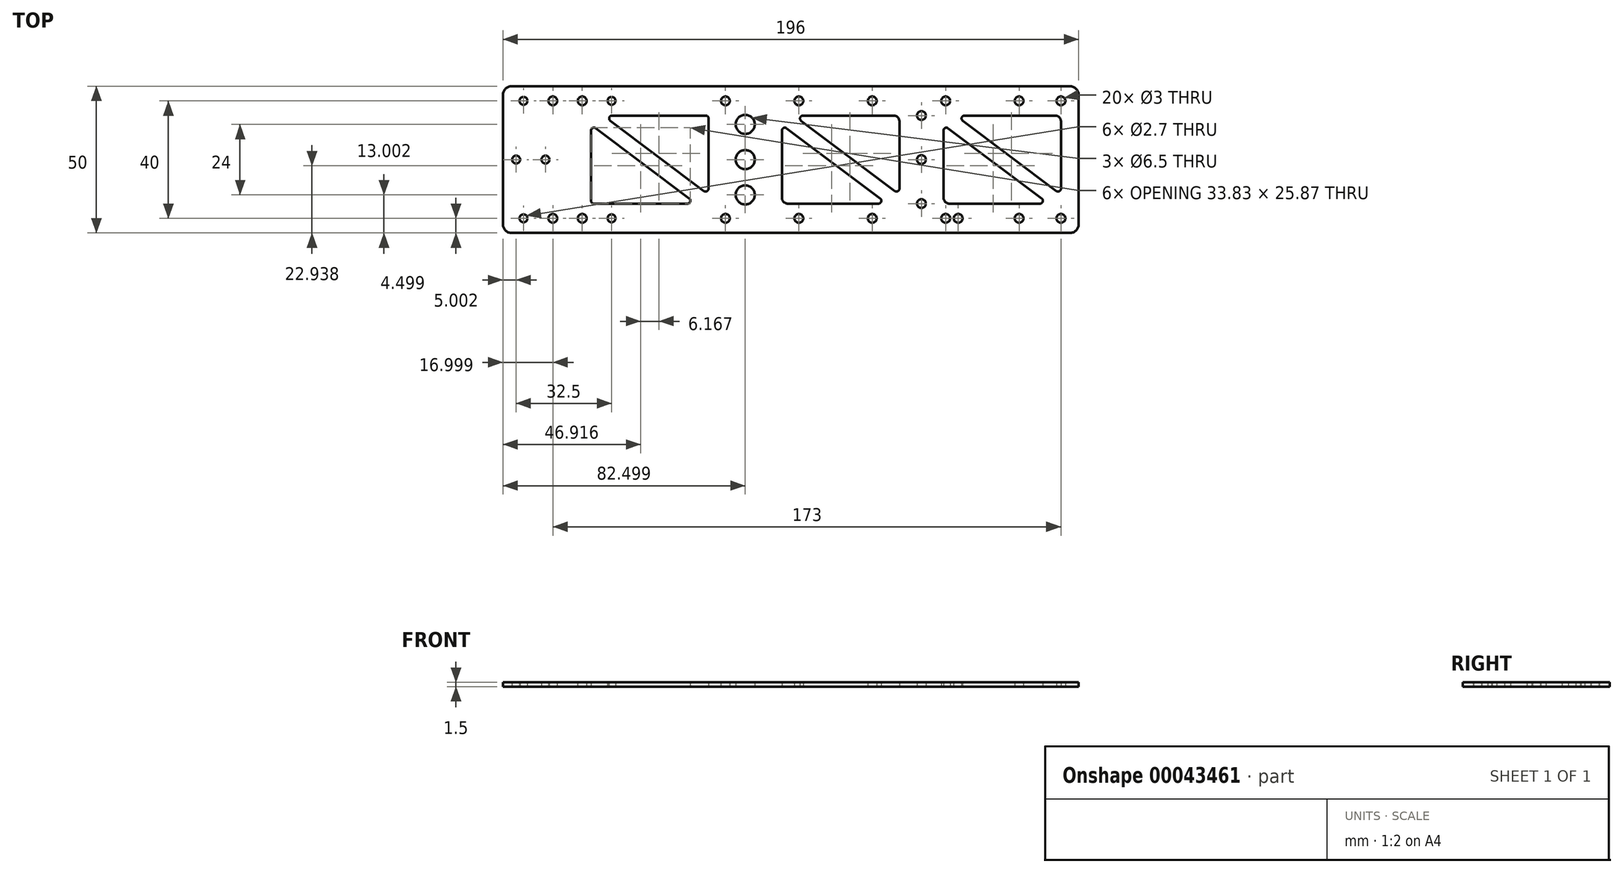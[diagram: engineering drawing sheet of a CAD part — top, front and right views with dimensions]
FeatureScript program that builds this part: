
annotation { "Feature Type Name" : "Feature", "Feature Type Description" : "" }
export const myFeature = defineFeature(function(context is Context, id is Id, definition is map)
    precondition{}
    {
        {
            var Q0;
            Q0=qCreatedBy(makeId("Top.planeOp"),FACE);
            var sketch = newSketch(context, id + "F0", { "sketchPlane" : qUnion([Q0])});
            skLineSegment(sketch, "E0.bottom", {"start": v(-128.11, 727.82) * mm, "end": v(61.89, 727.82) * mm});
            skLineSegment(sketch, "E0.top", {"start": v(-128.11, 677.82) * mm, "end": v(61.89, 677.82) * mm});
            skLineSegment(sketch, "E0.left", {"start": v(-131.11, 724.82) * mm, "end": v(-131.11, 680.82) * mm});
            skLineSegment(sketch, "E0.right", {"start": v(64.89, 724.82) * mm, "end": v(64.89, 680.82) * mm});
            skLineSegment(sketch, "E1", {"start": v(-131.11, 702.82) * mm, "end": v(64.89, 702.82) * mm});
            skCircle(sketch, "E2", {"center": v(-114.11, 722.82) * mm, "radius": 1.5 * mm});
            skCircle(sketch, "E3", {"center": v(-55.36, 722.82) * mm, "radius": 1.5 * mm});
            skCircle(sketch, "E4", {"center": v(23.89, 722.82) * mm, "radius": 1.5 * mm});
            skCircle(sketch, "E5", {"center": v(58.89, 722.82) * mm, "radius": 1.5 * mm});
            skCircle(sketch, "E6.MirrorC", {"center": v(58.89, 682.82) * mm, "radius": 1.5 * mm});
            skCircle(sketch, "E7.MirrorC", {"center": v(23.89, 682.82) * mm, "radius": 1.5 * mm});
            skCircle(sketch, "E8.MirrorC", {"center": v(-55.36, 682.82) * mm, "radius": 1.5 * mm});
            skCircle(sketch, "E9.MirrorC", {"center": v(-114.11, 682.82) * mm, "radius": 1.5 * mm});
            skCircle(sketch, "E10.MirrorC", {"center": v(-94.11, 682.82) * mm, "radius": 1.35 * mm});
            skPoint(sketch, "E11.visualSharp", {"position": v(64.89, 727.82) * mm});
            skArc(sketch, "E11.filletArc", {"start": v(64.89, 724.82) * mm, "mid": v(64.01, 726.94) * mm, "end": v(61.89, 727.82) * mm});
            skPoint(sketch, "E12.visualSharp", {"position": v(64.89, 677.82) * mm});
            skArc(sketch, "E12.filletArc", {"start": v(61.89, 677.82) * mm, "mid": v(64.01, 678.7) * mm, "end": v(64.89, 680.82) * mm});
            skLineSegment(sketch, "E13.bottom", {"start": v(56.89, 717.82) * mm, "end": v(20.89, 717.82) * mm});
            skLineSegment(sketch, "E13.top", {"start": v(56.89, 687.82) * mm, "end": v(20.89, 687.82) * mm});
            skLineSegment(sketch, "E13.left", {"start": v(58.89, 715.82) * mm, "end": v(58.89, 689.82) * mm});
            skLineSegment(sketch, "E13.right", {"start": v(18.89, 715.82) * mm, "end": v(18.89, 689.82) * mm});
            skLineSegment(sketch, "E14.bottom", {"start": v(1.89, 717.82) * mm, "end": v(-34.11, 717.82) * mm});
            skLineSegment(sketch, "E14.top", {"start": v(1.89, 687.82) * mm, "end": v(-34.11, 687.82) * mm});
            skLineSegment(sketch, "E14.left", {"start": v(3.89, 715.82) * mm, "end": v(3.89, 689.82) * mm});
            skLineSegment(sketch, "E14.right", {"start": v(-36.11, 715.82) * mm, "end": v(-36.11, 689.82) * mm});
            skLineSegment(sketch, "E15.bottom", {"start": v(-62.11, 717.82) * mm, "end": v(-98.11, 717.82) * mm});
            skLineSegment(sketch, "E15.top", {"start": v(-64.11, 687.82) * mm, "end": v(-100.11, 687.82) * mm});
            skLineSegment(sketch, "E15.left", {"start": v(-61.11, 716.82) * mm, "end": v(-61.11, 690.82) * mm});
            skLineSegment(sketch, "E15.right", {"start": v(-101.11, 714.82) * mm, "end": v(-101.11, 688.82) * mm});
            skPoint(sketch, "E16.visualSharp", {"position": v(-101.11, 717.82) * mm});
            skArc(sketch, "E16.filletArc", {"start": v(-98.11, 717.82) * mm, "mid": v(-100.23, 716.94) * mm, "end": v(-101.11, 714.82) * mm});
            skPoint(sketch, "E17.visualSharp", {"position": v(-101.11, 687.82) * mm});
            skArc(sketch, "E17.filletArc", {"start": v(-101.11, 688.82) * mm, "mid": v(-100.82, 688.12) * mm, "end": v(-100.11, 687.82) * mm});
            skPoint(sketch, "E18.visualSharp", {"position": v(-131.11, 727.82) * mm});
            skArc(sketch, "E18.filletArc", {"start": v(-128.11, 727.82) * mm, "mid": v(-130.23, 726.94) * mm, "end": v(-131.11, 724.82) * mm});
            skPoint(sketch, "E19.visualSharp", {"position": v(-131.11, 677.82) * mm});
            skArc(sketch, "E19.filletArc", {"start": v(-131.11, 680.82) * mm, "mid": v(-130.23, 678.7) * mm, "end": v(-128.11, 677.82) * mm});
            skCircle(sketch, "E20", {"center": v(-124.11, 722.82) * mm, "radius": 1.35 * mm});
            skCircle(sketch, "E21", {"center": v(-104.11, 722.82) * mm, "radius": 1.5 * mm});
            skPoint(sketch, "E22.visualSharp", {"position": v(-61.11, 717.82) * mm});
            skArc(sketch, "E22.filletArc", {"start": v(-61.11, 716.82) * mm, "mid": v(-61.4, 717.53) * mm, "end": v(-62.11, 717.82) * mm});
            skPoint(sketch, "E23.visualSharp", {"position": v(-61.11, 687.82) * mm});
            skArc(sketch, "E23.filletArc", {"start": v(-64.11, 687.82) * mm, "mid": v(-61.99, 688.7) * mm, "end": v(-61.11, 690.82) * mm});
            skCircle(sketch, "E24", {"center": v(-48.61, 714.82) * mm, "radius": 3.25 * mm});
            skCircle(sketch, "E25", {"center": v(-48.61, 702.82) * mm, "radius": 3.25 * mm});
            skCircle(sketch, "E26", {"center": v(-48.61, 690.82) * mm, "radius": 3.25 * mm});
            skLineSegment(sketch, "E27", {"start": v(-101.11, 717.82) * mm, "end": v(-61.11, 687.82) * mm});
            skLineSegment(sketch, "E28", {"start": v(-96.94, 717.82) * mm, "end": v(-61.11, 690.95) * mm});
            skLineSegment(sketch, "E29", {"start": v(-101.11, 714.7) * mm, "end": v(-65.28, 687.82) * mm});
            skCircle(sketch, "E30", {"center": v(-93.94, 716.82) * mm, "radius": 1 * mm});
            skCircle(sketch, "E31", {"center": v(-62.11, 692.95) * mm, "radius": 1 * mm});
            skCircle(sketch, "E32", {"center": v(-68.28, 688.82) * mm, "radius": 1 * mm});
            skCircle(sketch, "E33", {"center": v(-100.11, 712.7) * mm, "radius": 1 * mm});
            skCircle(sketch, "E34", {"center": v(11.39, 702.82) * mm, "radius": 1.5 * mm});
            skCircle(sketch, "E35", {"center": v(11.39, 717.82) * mm, "radius": 1.5 * mm});
            skCircle(sketch, "E36", {"center": v(11.39, 687.82) * mm, "radius": 1.5 * mm});
            skPoint(sketch, "E37.visualSharp", {"position": v(-36.11, 717.82) * mm});
            skArc(sketch, "E37.filletArc", {"start": v(-34.11, 717.82) * mm, "mid": v(-35.53, 717.24) * mm, "end": v(-36.11, 715.82) * mm});
            skPoint(sketch, "E38.visualSharp", {"position": v(-36.11, 687.82) * mm});
            skArc(sketch, "E38.filletArc", {"start": v(-36.11, 689.82) * mm, "mid": v(-35.53, 688.4) * mm, "end": v(-34.11, 687.82) * mm});
            skPoint(sketch, "E39.visualSharp", {"position": v(3.89, 717.82) * mm});
            skArc(sketch, "E39.filletArc", {"start": v(3.89, 715.82) * mm, "mid": v(3.3, 717.24) * mm, "end": v(1.89, 717.82) * mm});
            skPoint(sketch, "E40.visualSharp", {"position": v(3.89, 687.82) * mm});
            skArc(sketch, "E40.filletArc", {"start": v(1.89, 687.82) * mm, "mid": v(3.3, 688.4) * mm, "end": v(3.89, 689.82) * mm});
            skPoint(sketch, "E41.visualSharp", {"position": v(18.89, 717.82) * mm});
            skArc(sketch, "E41.filletArc", {"start": v(20.89, 717.82) * mm, "mid": v(19.47, 717.24) * mm, "end": v(18.89, 715.82) * mm});
            skPoint(sketch, "E42.visualSharp", {"position": v(58.89, 717.82) * mm});
            skArc(sketch, "E42.filletArc", {"start": v(58.89, 715.82) * mm, "mid": v(58.3, 717.24) * mm, "end": v(56.89, 717.82) * mm});
            skPoint(sketch, "E43.visualSharp", {"position": v(18.89, 687.82) * mm});
            skArc(sketch, "E43.filletArc", {"start": v(18.89, 689.82) * mm, "mid": v(19.47, 688.4) * mm, "end": v(20.89, 687.82) * mm});
            skPoint(sketch, "E44.visualSharp", {"position": v(58.89, 687.82) * mm});
            skArc(sketch, "E44.filletArc", {"start": v(56.89, 687.82) * mm, "mid": v(58.3, 688.4) * mm, "end": v(58.89, 689.82) * mm});
            skLineSegment(sketch, "E45", {"start": v(-36.11, 717.82) * mm, "end": v(3.89, 687.82) * mm});
            skLineSegment(sketch, "E46", {"start": v(-31.94, 717.82) * mm, "end": v(3.89, 690.95) * mm});
            skLineSegment(sketch, "E47", {"start": v(-36.11, 714.7) * mm, "end": v(-0.28, 687.82) * mm});
            skLineSegment(sketch, "E48", {"start": v(18.89, 717.82) * mm, "end": v(58.89, 687.82) * mm});
            skLineSegment(sketch, "E49", {"start": v(23.06, 717.82) * mm, "end": v(58.89, 690.95) * mm});
            skLineSegment(sketch, "E50", {"start": v(18.89, 714.7) * mm, "end": v(54.72, 687.82) * mm});
            skCircle(sketch, "E51", {"center": v(-28.94, 716.82) * mm, "radius": 1 * mm});
            skCircle(sketch, "E52", {"center": v(2.89, 692.95) * mm, "radius": 1 * mm});
            skCircle(sketch, "E53", {"center": v(-35.11, 712.7) * mm, "radius": 1 * mm});
            skCircle(sketch, "E54", {"center": v(-3.28, 688.82) * mm, "radius": 1 * mm});
            skCircle(sketch, "E55", {"center": v(19.89, 712.7) * mm, "radius": 1 * mm});
            skCircle(sketch, "E56", {"center": v(26.06, 716.82) * mm, "radius": 1 * mm});
            skCircle(sketch, "E57", {"center": v(57.89, 692.95) * mm, "radius": 1 * mm});
            skCircle(sketch, "E58", {"center": v(51.72, 688.82) * mm, "radius": 1 * mm});
            skCircle(sketch, "E59.MirrorC", {"center": v(-124.11, 682.82) * mm, "radius": 1.35 * mm});
            skCircle(sketch, "E60.MirrorC", {"center": v(-104.11, 682.82) * mm, "radius": 1.5 * mm});
            skCircle(sketch, "E61", {"center": v(-30.36, 722.82) * mm, "radius": 1.5 * mm});
            skCircle(sketch, "E62", {"center": v(-5.36, 722.82) * mm, "radius": 1.5 * mm});
            skCircle(sketch, "E63", {"center": v(19.64, 722.82) * mm, "radius": 1.5 * mm});
            skCircle(sketch, "E64", {"center": v(44.64, 722.82) * mm, "radius": 1.5 * mm});
            skCircle(sketch, "E65.MirrorC", {"center": v(-30.36, 682.82) * mm, "radius": 1.5 * mm});
            skCircle(sketch, "E66.MirrorC", {"center": v(19.64, 682.82) * mm, "radius": 1.5 * mm});
            skCircle(sketch, "E67.MirrorC", {"center": v(44.64, 682.82) * mm, "radius": 1.5 * mm});
            skCircle(sketch, "E68.MirrorC", {"center": v(-5.36, 682.82) * mm, "radius": 1.5 * mm});
            skCircle(sketch, "E69", {"center": v(-94.11, 722.82) * mm, "radius": 1.35 * mm});
            skCircle(sketch, "E70", {"center": v(-116.61, 702.82) * mm, "radius": 1.35 * mm});
            skCircle(sketch, "E71", {"center": v(-126.61, 702.82) * mm, "radius": 1.35 * mm});
            skSolve(sketch);
        }
        {
            var Q0;
            Q0=qSketchRegion(id+"F0",true);
            var Q1;
            {var subQ2=sQuery(id+"F0.wireOp",EDGE,"54195129-87a9-453f-ad2e-ab01bb990cc77.MirrorCS");Q1=makeQuery(id+"F0.imprint","IMPRINT",FACE,{"disambiguationData":[TD([[makeQuery(id+"F0.imprint","IMPRINT",EDGE,{"derivedFrom":subQ2}),-1.0]])]});}
            var Q2;
            {var subQ2=sQuery(id+"F0.wireOp",EDGE,"54195129-87a9-453f-ad2e-ab01bb990cc712.MirrorCS");Q2=makeQuery(id+"F0.imprint","IMPRINT",FACE,{"disambiguationData":[TD([[makeQuery(id+"F0.imprint","IMPRINT",EDGE,{"derivedFrom":subQ2}),1.0]])]});}
            var Q3;
            {var subQ0=sQuery(id+"F0.wireOp",EDGE,"54195129-87a9-453f-ad2e-ab01bb990cc74.MirrorCS");Q3=makeQuery(id+"F0.imprint","IMPRINT",FACE,{"disambiguationData":[TD([[makeQuery(id+"F0.imprint","IMPRINT",EDGE,{"derivedFrom":subQ0}),1.0]])]});}
            var Q4;
            {var subQ0=sQuery(id+"F0.wireOp",EDGE,"54195129-87a9-453f-ad2e-ab01bb990cc78.MirrorCS");Q4=makeQuery(id+"F0.imprint","IMPRINT",FACE,{"disambiguationData":[TD([[makeQuery(id+"F0.imprint","IMPRINT",EDGE,{"derivedFrom":subQ0}),1.0]])]});}
            var Q5;
            {var subQ0=sQuery(id+"F0.wireOp",EDGE,"BcqDGKqa-283v-lT3W-7pAC-w2yEAsonch5c");Q5=makeQuery(id+"F0.imprint","IMPRINT",FACE,{"disambiguationData":[TD([[makeQuery(id+"F0.imprint","IMPRINT",EDGE,{"derivedFrom":subQ0}),-1.0]])]});}
            var Q6;
            {var subQ2=sQuery(id+"F0.wireOp",EDGE,"ShlW986k-ajFc-8yeV-3Gdn-sOu9Hpu2vA3Z");Q6=makeQuery(id+"F0.imprint","IMPRINT",FACE,{"disambiguationData":[TD([[makeQuery(id+"F0.imprint","IMPRINT",EDGE,{"derivedFrom":subQ2}),-1.0]])]});}
            var Q7;
            {var subQ2=sQuery(id+"F0.wireOp",EDGE,"w6zGlNOe-O8Z4-KzDY-468z-d0JdHNhxJH18");Q7=makeQuery(id+"F0.imprint","IMPRINT",FACE,{"disambiguationData":[TD([[makeQuery(id+"F0.imprint","IMPRINT",EDGE,{"derivedFrom":subQ2}),-1.0]])]});}
            var Q8;
            {var subQ0=sQuery(id+"F0.wireOp",EDGE,"v6rJk5rU-W7GU-l5Cy-b2Ia-JKdmIbJVq7ve");Q8=makeQuery(id+"F0.imprint","IMPRINT",FACE,{"disambiguationData":[TD([[makeQuery(id+"F0.imprint","IMPRINT",EDGE,{"derivedFrom":subQ0}),-1.0]])]});}
            var Q9;
            {var subQ0=sQuery(id+"F0.wireOp",EDGE,"e183a9b5-fc32-46b4-9d97-09565e521898.right");var subQ1=sQuery(id+"F0.wireOp",EDGE,"wU84TTQi-j5bG-VybG-7onn-GEVu1O6ivYgl");var subQ2=makeQuery(id+"F0.imprint","INTERSECT",VERTEX,{"derivedFrom":[subQ1,subQ0]});Q9=makeQuery(id+"F0.imprint","IMPRINT",FACE,{"disambiguationData":[TD([[makeQuery(id+"F0.imprint","IMPRINT",EDGE,{"disambiguationData":[TD([[subQ2,-1.0]])],"derivedFrom":subQ1}),-1.0]])]});}
            var Q10;
            {var subQ0=sQuery(id+"F0.wireOp",EDGE,"e183a9b5-fc32-46b4-9d97-09565e521898.right");var subQ1=sQuery(id+"F0.wireOp",EDGE,"wU84TTQi-j5bG-VybG-7onn-GEVu1O6ivYgl");var subQ2=makeQuery(id+"F0.imprint","INTERSECT",VERTEX,{"derivedFrom":[subQ1,subQ0]});Q10=makeQuery(id+"F0.imprint","IMPRINT",FACE,{"disambiguationData":[TD([[makeQuery(id+"F0.imprint","IMPRINT",EDGE,{"disambiguationData":[TD([[subQ2,-1.0]])],"derivedFrom":subQ1}),1.0]])]});}
            var Q11;
            Q11=makeQuery(id+"F0.imprint","IMPRINT",FACE,{"disambiguationData":[TD([[makeQuery(id+"F0.imprint","IMPRINT",EDGE,{"derivedFrom":sQuery(id+"F0.wireOp",EDGE,"E4")}),1.0]])]});
            var Q12;
            Q12=makeQuery(id+"F0.imprint","IMPRINT",FACE,{"disambiguationData":[TD([[makeQuery(id+"F0.imprint","IMPRINT",EDGE,{"derivedFrom":sQuery(id+"F0.wireOp",EDGE,"E7.MirrorC")}),-1.0]])]});
            var Q13;
            {var subQ0=sQuery(id+"F0.wireOp",EDGE,"E29");var subQ6=sQuery(id+"F0.wireOp",EDGE,"E1");var subQ8=makeQuery(id+"F0.imprint","INTERSECT",VERTEX,{"derivedFrom":[subQ6,subQ0]});Q13=makeQuery(id+"F0.imprint","IMPRINT",FACE,{"disambiguationData":[TD([[makeQuery(id+"F0.imprint","IMPRINT",EDGE,{"disambiguationData":[TD([[subQ8,-1.0]])],"derivedFrom":subQ6}),1.0]])]});}
            var Q14;
            {var subQ0=sQuery(id+"F0.wireOp",EDGE,"E27");var subQ3=sQuery(id+"F0.wireOp",EDGE,"E1");var subQ4=makeQuery(id+"F0.imprint","INTERSECT",VERTEX,{"derivedFrom":[subQ3,subQ0]});Q14=makeQuery(id+"F0.imprint","IMPRINT",FACE,{"disambiguationData":[TD([[makeQuery(id+"F0.imprint","IMPRINT",EDGE,{"disambiguationData":[TD([[subQ4,-1.0]])],"derivedFrom":subQ3}),1.0]])]});}
            var Q15;
            {var subQ1=sQuery(id+"F0.wireOp",EDGE,"E1");var subQ4=sQuery(id+"F0.wireOp",EDGE,"E27");var subQ7=makeQuery(id+"F0.imprint","INTERSECT",VERTEX,{"derivedFrom":[subQ1,subQ4]});Q15=makeQuery(id+"F0.imprint","IMPRINT",FACE,{"disambiguationData":[TD([[makeQuery(id+"F0.imprint","IMPRINT",EDGE,{"disambiguationData":[TD([[subQ7,-1.0]])],"derivedFrom":subQ1}),-1.0]])]});}
            var Q16;
            {var subQ3=sQuery(id+"F0.wireOp",EDGE,"E1");var subQ7=sQuery(id+"F0.wireOp",EDGE,"E29");var subQ9=makeQuery(id+"F0.imprint","INTERSECT",VERTEX,{"derivedFrom":[subQ3,subQ7]});Q16=makeQuery(id+"F0.imprint","IMPRINT",FACE,{"disambiguationData":[TD([[makeQuery(id+"F0.imprint","IMPRINT",EDGE,{"disambiguationData":[TD([[subQ9,-1.0]])],"derivedFrom":subQ3}),-1.0]])]});}
            var Q17;
            {var subQ0=sQuery(id+"F0.wireOp",EDGE,"E23.filletArc");var subQ1=sQuery(id+"F0.wireOp",EDGE,"E15.left");var subQ2=makeQuery(id+"F0.imprint","INTERSECT",VERTEX,{"derivedFrom":[subQ1,subQ0]});Q17=makeQuery(id+"F0.imprint","IMPRINT",FACE,{"disambiguationData":[TD([[makeQuery(id+"F0.imprint","IMPRINT",EDGE,{"disambiguationData":[TD([[subQ2,1.0]])],"derivedFrom":subQ1}),-1.0]])]});}
            var Q18;
            {var subQ0=sQuery(id+"F0.wireOp",EDGE,"E29");var subQ1=sQuery(id+"F0.wireOp",EDGE,"E15.top");var subQ2=makeQuery(id+"F0.imprint","INTERSECT",VERTEX,{"derivedFrom":[subQ1,subQ0]});Q18=makeQuery(id+"F0.imprint","IMPRINT",FACE,{"disambiguationData":[TD([[makeQuery(id+"F0.imprint","IMPRINT",EDGE,{"disambiguationData":[TD([[subQ2,-1.0]])],"derivedFrom":subQ1}),-1.0]])]});}
            var Q19;
            {var subQ0=sQuery(id+"F0.wireOp",EDGE,"E28");var subQ1=sQuery(id+"F0.wireOp",EDGE,"E15.bottom");var subQ2=makeQuery(id+"F0.imprint","INTERSECT",VERTEX,{"derivedFrom":[subQ1,subQ0]});Q19=makeQuery(id+"F0.imprint","IMPRINT",FACE,{"disambiguationData":[TD([[makeQuery(id+"F0.imprint","IMPRINT",EDGE,{"disambiguationData":[TD([[subQ2,1.0]])],"derivedFrom":subQ1}),1.0]])]});}
            var Q20;
            {var subQ0=sQuery(id+"F0.wireOp",EDGE,"E16.filletArc");var subQ1=sQuery(id+"F0.wireOp",EDGE,"E15.right");var subQ2=makeQuery(id+"F0.imprint","INTERSECT",VERTEX,{"derivedFrom":[subQ1,subQ0]});Q20=makeQuery(id+"F0.imprint","IMPRINT",FACE,{"disambiguationData":[TD([[makeQuery(id+"F0.imprint","IMPRINT",EDGE,{"disambiguationData":[TD([[subQ2,-1.0]])],"derivedFrom":subQ1}),1.0]])]});}
            var Q21;
            {var subQ0=sQuery(id+"F0.wireOp",EDGE,"E45");var subQ3=sQuery(id+"F0.wireOp",EDGE,"E1");var subQ4=makeQuery(id+"F0.imprint","INTERSECT",VERTEX,{"derivedFrom":[subQ3,subQ0]});Q21=makeQuery(id+"F0.imprint","IMPRINT",FACE,{"disambiguationData":[TD([[makeQuery(id+"F0.imprint","IMPRINT",EDGE,{"disambiguationData":[TD([[subQ4,-1.0]])],"derivedFrom":subQ3}),1.0]])]});}
            var Q22;
            {var subQ3=sQuery(id+"F0.wireOp",EDGE,"E1");var subQ7=sQuery(id+"F0.wireOp",EDGE,"E47");var subQ9=makeQuery(id+"F0.imprint","INTERSECT",VERTEX,{"derivedFrom":[subQ3,subQ7]});Q22=makeQuery(id+"F0.imprint","IMPRINT",FACE,{"disambiguationData":[TD([[makeQuery(id+"F0.imprint","IMPRINT",EDGE,{"disambiguationData":[TD([[subQ9,-1.0]])],"derivedFrom":subQ3}),1.0]])]});}
            var Q23;
            {var subQ3=sQuery(id+"F0.wireOp",EDGE,"E1");var subQ7=sQuery(id+"F0.wireOp",EDGE,"E47");var subQ9=makeQuery(id+"F0.imprint","INTERSECT",VERTEX,{"derivedFrom":[subQ3,subQ7]});Q23=makeQuery(id+"F0.imprint","IMPRINT",FACE,{"disambiguationData":[TD([[makeQuery(id+"F0.imprint","IMPRINT",EDGE,{"disambiguationData":[TD([[subQ9,-1.0]])],"derivedFrom":subQ3}),-1.0]])]});}
            var Q24;
            {var subQ3=sQuery(id+"F0.wireOp",EDGE,"E45");var subQ7=sQuery(id+"F0.wireOp",EDGE,"E1");var subQ8=makeQuery(id+"F0.imprint","INTERSECT",VERTEX,{"derivedFrom":[subQ7,subQ3]});Q24=makeQuery(id+"F0.imprint","IMPRINT",FACE,{"disambiguationData":[TD([[makeQuery(id+"F0.imprint","IMPRINT",EDGE,{"disambiguationData":[TD([[subQ8,-1.0]])],"derivedFrom":subQ7}),-1.0]])]});}
            var Q25;
            {var subQ0=sQuery(id+"F0.wireOp",EDGE,"E47");var subQ1=sQuery(id+"F0.wireOp",EDGE,"E14.top");var subQ2=makeQuery(id+"F0.imprint","INTERSECT",VERTEX,{"derivedFrom":[subQ1,subQ0]});Q25=makeQuery(id+"F0.imprint","IMPRINT",FACE,{"disambiguationData":[TD([[makeQuery(id+"F0.imprint","IMPRINT",EDGE,{"disambiguationData":[TD([[subQ2,-1.0]])],"derivedFrom":subQ1}),-1.0]])]});}
            var Q26;
            {var subQ0=sQuery(id+"F0.wireOp",EDGE,"E46");var subQ1=sQuery(id+"F0.wireOp",EDGE,"E14.left");var subQ2=makeQuery(id+"F0.imprint","INTERSECT",VERTEX,{"derivedFrom":[subQ1,subQ0]});Q26=makeQuery(id+"F0.imprint","IMPRINT",FACE,{"disambiguationData":[TD([[makeQuery(id+"F0.imprint","IMPRINT",EDGE,{"disambiguationData":[TD([[subQ2,1.0]])],"derivedFrom":subQ1}),-1.0]])]});}
            var Q27;
            {var subQ0=sQuery(id+"F0.wireOp",EDGE,"E46");var subQ1=sQuery(id+"F0.wireOp",EDGE,"E14.bottom");var subQ2=makeQuery(id+"F0.imprint","INTERSECT",VERTEX,{"derivedFrom":[subQ1,subQ0]});Q27=makeQuery(id+"F0.imprint","IMPRINT",FACE,{"disambiguationData":[TD([[makeQuery(id+"F0.imprint","IMPRINT",EDGE,{"disambiguationData":[TD([[subQ2,1.0]])],"derivedFrom":subQ1}),1.0]])]});}
            var Q28;
            {var subQ0=sQuery(id+"F0.wireOp",EDGE,"E47");var subQ1=sQuery(id+"F0.wireOp",EDGE,"E14.right");var subQ2=makeQuery(id+"F0.imprint","INTERSECT",VERTEX,{"derivedFrom":[subQ1,subQ0]});Q28=makeQuery(id+"F0.imprint","IMPRINT",FACE,{"disambiguationData":[TD([[makeQuery(id+"F0.imprint","IMPRINT",EDGE,{"disambiguationData":[TD([[subQ2,-1.0]])],"derivedFrom":subQ1}),1.0]])]});}
            var Q29;
            {var subQ3=sQuery(id+"F0.wireOp",EDGE,"E1");var subQ5=sQuery(id+"F0.wireOp",EDGE,"E50");var subQ6=makeQuery(id+"F0.imprint","INTERSECT",VERTEX,{"derivedFrom":[subQ3,subQ5]});Q29=makeQuery(id+"F0.imprint","IMPRINT",FACE,{"disambiguationData":[TD([[makeQuery(id+"F0.imprint","IMPRINT",EDGE,{"disambiguationData":[TD([[subQ6,-1.0]])],"derivedFrom":subQ3}),1.0]])]});}
            var Q30;
            {var subQ0=sQuery(id+"F0.wireOp",EDGE,"E48");var subQ3=sQuery(id+"F0.wireOp",EDGE,"E1");var subQ4=makeQuery(id+"F0.imprint","INTERSECT",VERTEX,{"derivedFrom":[subQ3,subQ0]});Q30=makeQuery(id+"F0.imprint","IMPRINT",FACE,{"disambiguationData":[TD([[makeQuery(id+"F0.imprint","IMPRINT",EDGE,{"disambiguationData":[TD([[subQ4,-1.0]])],"derivedFrom":subQ3}),1.0]])]});}
            var Q31;
            {var subQ3=sQuery(id+"F0.wireOp",EDGE,"E1");var subQ5=sQuery(id+"F0.wireOp",EDGE,"E50");var subQ6=makeQuery(id+"F0.imprint","INTERSECT",VERTEX,{"derivedFrom":[subQ3,subQ5]});Q31=makeQuery(id+"F0.imprint","IMPRINT",FACE,{"disambiguationData":[TD([[makeQuery(id+"F0.imprint","IMPRINT",EDGE,{"disambiguationData":[TD([[subQ6,-1.0]])],"derivedFrom":subQ3}),-1.0]])]});}
            var Q32;
            {var subQ3=sQuery(id+"F0.wireOp",EDGE,"E48");var subQ5=sQuery(id+"F0.wireOp",EDGE,"E1");var subQ6=makeQuery(id+"F0.imprint","INTERSECT",VERTEX,{"derivedFrom":[subQ5,subQ3]});Q32=makeQuery(id+"F0.imprint","IMPRINT",FACE,{"disambiguationData":[TD([[makeQuery(id+"F0.imprint","IMPRINT",EDGE,{"disambiguationData":[TD([[subQ6,-1.0]])],"derivedFrom":subQ5}),-1.0]])]});}
            var Q33;
            {var subQ0=sQuery(id+"F0.wireOp",EDGE,"E49");var subQ1=sQuery(id+"F0.wireOp",EDGE,"E13.bottom");var subQ2=makeQuery(id+"F0.imprint","INTERSECT",VERTEX,{"derivedFrom":[subQ1,subQ0]});Q33=makeQuery(id+"F0.imprint","IMPRINT",FACE,{"disambiguationData":[TD([[makeQuery(id+"F0.imprint","IMPRINT",EDGE,{"disambiguationData":[TD([[subQ2,1.0]])],"derivedFrom":subQ1}),1.0]])]});}
            var Q34;
            {var subQ0=sQuery(id+"F0.wireOp",EDGE,"E50");var subQ1=sQuery(id+"F0.wireOp",EDGE,"E13.right");var subQ2=makeQuery(id+"F0.imprint","INTERSECT",VERTEX,{"derivedFrom":[subQ1,subQ0]});Q34=makeQuery(id+"F0.imprint","IMPRINT",FACE,{"disambiguationData":[TD([[makeQuery(id+"F0.imprint","IMPRINT",EDGE,{"disambiguationData":[TD([[subQ2,-1.0]])],"derivedFrom":subQ1}),1.0]])]});}
            var Q35;
            {var subQ0=sQuery(id+"F0.wireOp",EDGE,"E49");var subQ1=sQuery(id+"F0.wireOp",EDGE,"E13.left");var subQ2=makeQuery(id+"F0.imprint","INTERSECT",VERTEX,{"derivedFrom":[subQ1,subQ0]});Q35=makeQuery(id+"F0.imprint","IMPRINT",FACE,{"disambiguationData":[TD([[makeQuery(id+"F0.imprint","IMPRINT",EDGE,{"disambiguationData":[TD([[subQ2,1.0]])],"derivedFrom":subQ1}),-1.0]])]});}
            var Q36;
            {var subQ0=sQuery(id+"F0.wireOp",EDGE,"E50");var subQ1=sQuery(id+"F0.wireOp",EDGE,"E13.top");var subQ2=makeQuery(id+"F0.imprint","INTERSECT",VERTEX,{"derivedFrom":[subQ1,subQ0]});Q36=makeQuery(id+"F0.imprint","IMPRINT",FACE,{"disambiguationData":[TD([[makeQuery(id+"F0.imprint","IMPRINT",EDGE,{"disambiguationData":[TD([[subQ2,-1.0]])],"derivedFrom":subQ1}),-1.0]])]});}
            var Q37;
            {var subQ0=sQuery(id+"F0.wireOp",EDGE,"E28");var subQ1=sQuery(id+"F0.wireOp",EDGE,"E15.left");var subQ2=makeQuery(id+"F0.imprint","INTERSECT",VERTEX,{"derivedFrom":[subQ1,subQ0]});Q37=makeQuery(id+"F0.imprint","IMPRINT",FACE,{"disambiguationData":[TD([[makeQuery(id+"F0.imprint","IMPRINT",EDGE,{"disambiguationData":[TD([[subQ2,1.0]])],"derivedFrom":subQ1}),-1.0]])]});}
            var Q38;
            {var subQ0=sQuery(id+"F0.wireOp",EDGE,"E29");var subQ1=sQuery(id+"F0.wireOp",EDGE,"E15.right");var subQ2=makeQuery(id+"F0.imprint","INTERSECT",VERTEX,{"derivedFrom":[subQ1,subQ0]});Q38=makeQuery(id+"F0.imprint","IMPRINT",FACE,{"disambiguationData":[TD([[makeQuery(id+"F0.imprint","IMPRINT",EDGE,{"disambiguationData":[TD([[subQ2,-1.0]])],"derivedFrom":subQ1}),1.0]])]});}
            extrude(context, id + "F1", {"entities" : qUnion([Q0, Q1, Q2, Q3, Q4, Q5, Q6, Q7, Q8, Q9, Q10, Q11, Q12, Q13, Q14, Q15, Q16, Q17, Q18, Q19, Q20, Q21, Q22, Q23, Q24, Q25, Q26, Q27, Q28, Q29, Q30, Q31, Q32, Q33, Q34, Q35, Q36, Q37, Q38]), "depth" : 1.5 * mm});
        }
    });
